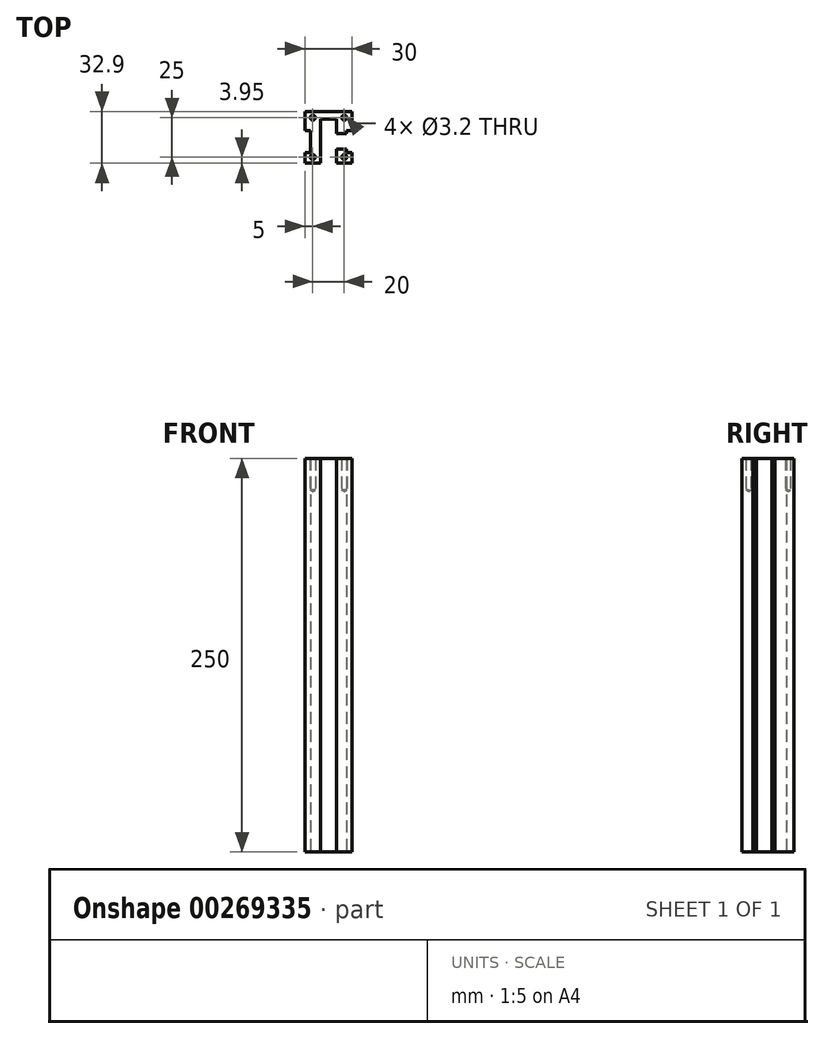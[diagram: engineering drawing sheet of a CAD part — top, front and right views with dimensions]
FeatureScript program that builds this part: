
annotation { "Feature Type Name" : "Feature", "Feature Type Description" : "" }
export const myFeature = defineFeature(function(context is Context, id is Id, definition is map)
    precondition{}
    {
        {
            var Q0;
            Q0=qCreatedBy(makeId("Top.planeOp"),FACE);
            var sketch = newSketch(context, id + "F0", { "sketchPlane" : qUnion([Q0])});
            skLineSegment(sketch, "E0", {"start": v(11.5, 2.45) * mm, "end": v(11.5, 4.45) * mm});
            skLineSegment(sketch, "E1", {"start": v(11.5, 4.45) * mm, "end": v(15, 4.45) * mm});
            skLineSegment(sketch, "E2", {"start": v(15, 4.45) * mm, "end": v(15, 16.45) * mm});
            skLineSegment(sketch, "E3", {"start": v(15, 16.45) * mm, "end": v(-15, 16.45) * mm});
            skLineSegment(sketch, "E4", {"start": v(-15, 16.45) * mm, "end": v(-15, 4.45) * mm});
            skLineSegment(sketch, "E5", {"start": v(-15, 4.45) * mm, "end": v(-11.5, 4.45) * mm});
            skLineSegment(sketch, "E6", {"start": v(-11.5, 4.45) * mm, "end": v(-11.5, -9.55) * mm});
            skLineSegment(sketch, "E7", {"start": v(-11.5, -9.55) * mm, "end": v(-15, -9.55) * mm});
            skLineSegment(sketch, "E8", {"start": v(-15, -9.55) * mm, "end": v(-15, -16.45) * mm});
            skLineSegment(sketch, "E9", {"start": v(-15, -16.45) * mm, "end": v(-5, -16.45) * mm});
            skLineSegment(sketch, "E10", {"start": v(-5, -16.45) * mm, "end": v(-5, 11.65) * mm});
            skLineSegment(sketch, "E11", {"start": v(-5, 11.65) * mm, "end": v(5, 11.65) * mm});
            skLineSegment(sketch, "E12", {"start": v(5, 11.65) * mm, "end": v(5, 2.45) * mm});
            skLineSegment(sketch, "E13", {"start": v(5, 2.45) * mm, "end": v(11.5, 2.45) * mm});
            skLineSegment(sketch, "E14", {"start": v(5, -7.45) * mm, "end": v(11.5, -7.45) * mm});
            skLineSegment(sketch, "E15", {"start": v(11.5, -7.45) * mm, "end": v(11.5, -9.55) * mm});
            skLineSegment(sketch, "E16", {"start": v(11.5, -9.55) * mm, "end": v(15, -9.55) * mm});
            skLineSegment(sketch, "E17", {"start": v(15, -9.55) * mm, "end": v(15, -16.45) * mm});
            skLineSegment(sketch, "E18", {"start": v(15, -16.45) * mm, "end": v(5, -16.45) * mm});
            skLineSegment(sketch, "E19", {"start": v(5, -16.45) * mm, "end": v(5, -7.45) * mm});
            skLineSegment(sketch, "E20", {"start": v(0, 16.45) * mm, "end": v(0, -16.45) * mm, "construction": true});
            skLineSegment(sketch, "E21", {"start": v(-5, -16.45) * mm, "end": v(5, -16.45) * mm, "construction": true});
            skLineSegment(sketch, "E22", {"start": v(15, 4.45) * mm, "end": v(15, -9.55) * mm, "construction": true});
            skSolve(sketch);
        }
        {
            var Q0;
            Q0=makeQuery(id+"F0.imprint","IMPRINT",FACE,{"disambiguationData":[TD([[makeQuery(id+"F0.imprint","IMPRINT",EDGE,{"derivedFrom":sQuery(id+"F0.wireOp",EDGE,"E0")}),1.0]])]});
            var Q1;
            Q1=makeQuery(id+"F0.imprint","IMPRINT",FACE,{"disambiguationData":[TD([[makeQuery(id+"F0.imprint","IMPRINT",EDGE,{"derivedFrom":sQuery(id+"F0.wireOp",EDGE,"E14")}),-1.0]])]});
            extrude(context, id + "F1", {"entities" : qUnion([Q0, Q1]), "depth" : 250 * mm});
        }
        {
            var Q0;
            Q0=makeQuery(id+"F1.opExtrude","CAP_FACE",FACE,{"disambiguationData":[OSD([sQuery(id+"F0.wireOp",EDGE,"E0"),sQuery(id+"F0.wireOp",EDGE,"E1"),sQuery(id+"F0.wireOp",EDGE,"E2"),sQuery(id+"F0.wireOp",EDGE,"E3"),sQuery(id+"F0.wireOp",EDGE,"E4"),sQuery(id+"F0.wireOp",EDGE,"E5"),sQuery(id+"F0.wireOp",EDGE,"E6"),sQuery(id+"F0.wireOp",EDGE,"E7"),sQuery(id+"F0.wireOp",EDGE,"E8"),sQuery(id+"F0.wireOp",EDGE,"E9"),sQuery(id+"F0.wireOp",EDGE,"E10"),sQuery(id+"F0.wireOp",EDGE,"E11"),sQuery(id+"F0.wireOp",EDGE,"E12"),sQuery(id+"F0.wireOp",EDGE,"E13")])],"isStart":false});
            var sketch = newSketch(context, id + "F2", { "sketchPlane" : qUnion([Q0])});
            skLineSegment(sketch, "E23", {"start": v(-10, 12.5) * mm, "end": v(10, 12.5) * mm, "construction": true});
            skLineSegment(sketch, "E24", {"start": v(10, 12.5) * mm, "end": v(10, -12.5) * mm, "construction": true});
            skLineSegment(sketch, "E25", {"start": v(10, -12.5) * mm, "end": v(-10, -12.5) * mm, "construction": true});
            skLineSegment(sketch, "E26", {"start": v(-10, -12.5) * mm, "end": v(-10, 12.5) * mm, "construction": true});
            skLineSegment(sketch, "E27", {"start": v(-10, 0) * mm, "end": v(10, 0) * mm, "construction": true});
            skLineSegment(sketch, "E28", {"start": v(0, 12.5) * mm, "end": v(0, -12.5) * mm, "construction": true});
            skPoint(sketch, "E28.endSnap0", {"position": v(0, -12.5) * mm});
            skSolve(sketch);
        }
        {
            var Q0;
            Q0=sQuery(id+"F2.wireOp",VERTEX,"E23.start");
            var Q1;
            Q1=sQuery(id+"F2.wireOp",VERTEX,"E24.start");
            var Q2;
            Q2=sQuery(id+"F2.wireOp",VERTEX,"E25.start");
            var Q3;
            Q3=sQuery(id+"F2.wireOp",VERTEX,"E26.start");
            var Q4;
            Q4=makeQuery(id+"F1.opExtrude","SWEPT_BODY",BODY,{"disambiguationData":[OSD([sQuery(id+"F0.wireOp",EDGE,"E0"),sQuery(id+"F0.wireOp",EDGE,"E1"),sQuery(id+"F0.wireOp",EDGE,"E2"),sQuery(id+"F0.wireOp",EDGE,"E3"),sQuery(id+"F0.wireOp",EDGE,"E4"),sQuery(id+"F0.wireOp",EDGE,"E5"),sQuery(id+"F0.wireOp",EDGE,"E6"),sQuery(id+"F0.wireOp",EDGE,"E7"),sQuery(id+"F0.wireOp",EDGE,"E8"),sQuery(id+"F0.wireOp",EDGE,"E9"),sQuery(id+"F0.wireOp",EDGE,"E10"),sQuery(id+"F0.wireOp",EDGE,"E11"),sQuery(id+"F0.wireOp",EDGE,"E12"),sQuery(id+"F0.wireOp",EDGE,"E13")])]});
            var Q5;
            Q5=makeQuery(id+"F1.opExtrude","SWEPT_BODY",BODY,{"disambiguationData":[OSD([sQuery(id+"F0.wireOp",EDGE,"E14"),sQuery(id+"F0.wireOp",EDGE,"E15"),sQuery(id+"F0.wireOp",EDGE,"E16"),sQuery(id+"F0.wireOp",EDGE,"E17"),sQuery(id+"F0.wireOp",EDGE,"E18"),sQuery(id+"F0.wireOp",EDGE,"E19")])]});
            hole(context, id + "F3", {"style" : HoleStyle.SIMPLE, "endStyle" : HoleEndStyle.BLIND, "standardTappedOrClearance" : lookupTablePath({ "standard" : "ISO", "engagement" : "75%", "pitch" : "0.75 mm", "size" : "M4", "type" : "Tapped" }), "standardBlindInLast" : lookupTablePath({ "standard" : "ISO", "engagement" : "75%", "pitch" : "0.75 mm", "size" : "M4", "type" : "Tapped" }), "holeDiameter" : 3.2 * mm, "holeDepth" : 20 * mm, "locations" : qUnion([Q0, Q1, Q2, Q3]), "scope" : qUnion([Q4, Q5])});
        }
    });
